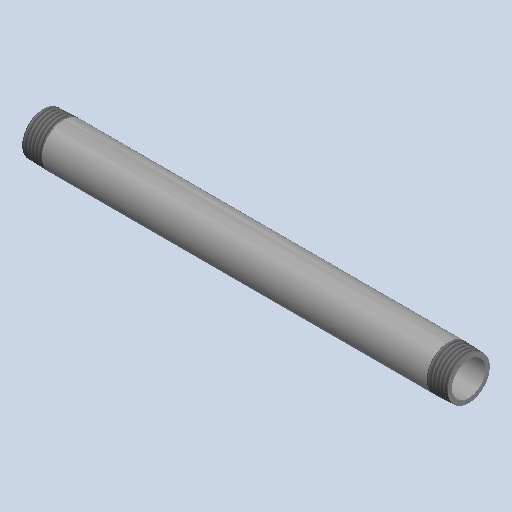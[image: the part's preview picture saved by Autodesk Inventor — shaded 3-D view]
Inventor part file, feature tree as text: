
AUTODESK INVENTOR PART (.ipt)
format: ipt  version: 2025 (Build 290162000, 162)  size: 186,880 bytes
history: native  units: mm (DEFAULTED — no unit token found)
features: other x8, revolve x1
ambient origin geometry x8: Origin, YZ Plane, XZ Plane, XY Plane, X Axis, Y Axis, Z Axis, Center Point
bodies: Solid1 (feature_tree)
feature tree (9):
  revolve  "Revolution1"  [1 undecoded]
  other  "Work Axis1"
  other  "Work Point5"
  other  "Work Axis2"
  other  "Work Point6"
  other  "Work Axis3"
  other  "Work Axis4"
  other  "Work Point7"
  other  "Work Point8"
note: 1 required parameter value undecoded (feature->parameter linkage not recoverable at this tier; creation-order binding heuristic only, values carry confidence <= 0.55)
